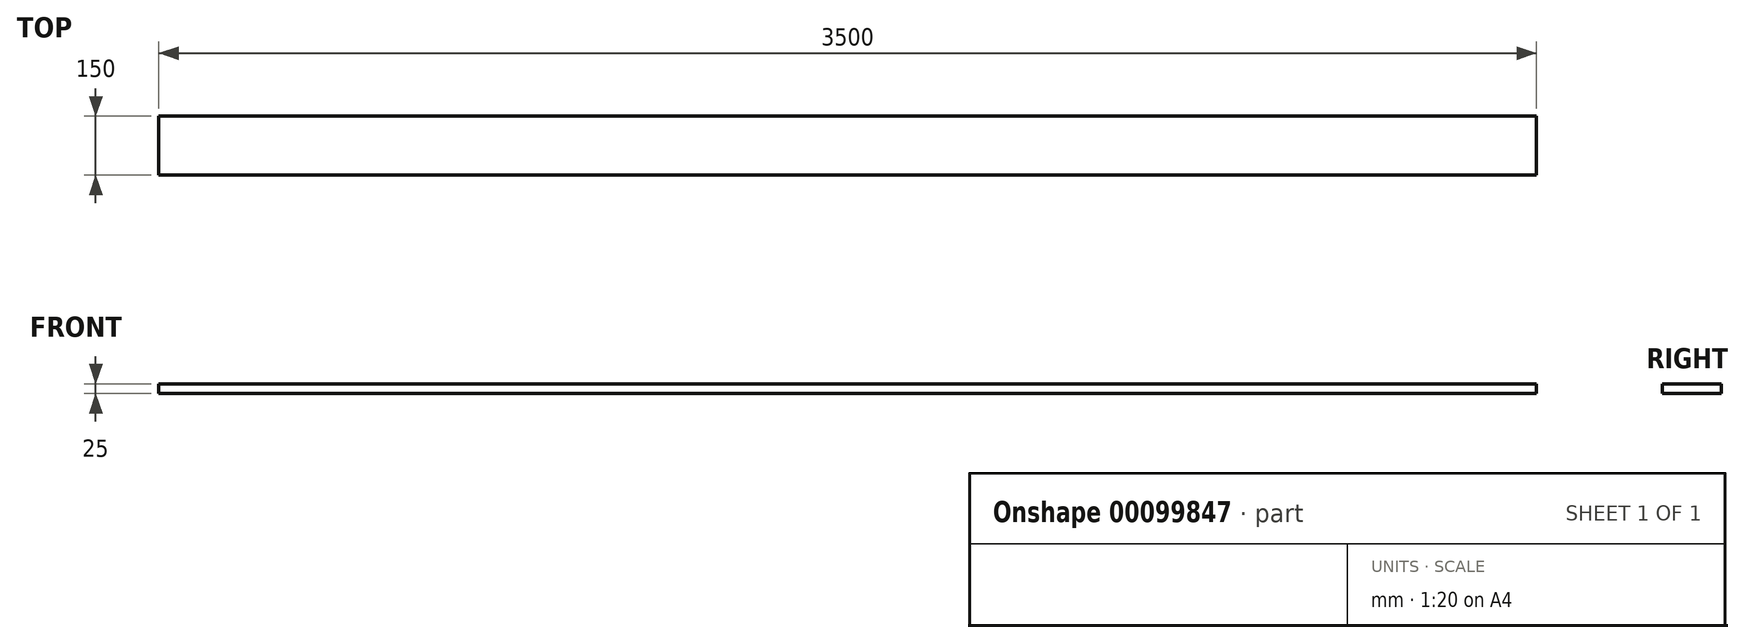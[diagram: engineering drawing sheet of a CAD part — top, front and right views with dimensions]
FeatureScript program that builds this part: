
annotation { "Feature Type Name" : "Feature", "Feature Type Description" : "" }
export const myFeature = defineFeature(function(context is Context, id is Id, definition is map)
    precondition{}
    {
        {
            var Q0;
            Q0=qCreatedBy(makeId("Top.planeOp"),FACE);
            var sketch = newSketch(context, id + "F0", { "sketchPlane" : qUnion([Q0])});
            skLineSegment(sketch, "E0.bottom", {"start": v(-1750, 0) * mm, "end": v(1750, 0) * mm});
            skLineSegment(sketch, "E0.top", {"start": v(-1750, -150) * mm, "end": v(1750, -150) * mm});
            skLineSegment(sketch, "E0.left", {"start": v(-1750, 0) * mm, "end": v(-1750, -150) * mm});
            skLineSegment(sketch, "E0.right", {"start": v(1750, 0) * mm, "end": v(1750, -150) * mm});
            skSolve(sketch);
        }
        {
            var Q0;
            Q0 = qSketchRegion(id + "F0", true);
            extrude(context, id + "F1", {"entities" : qUnion([Q0]), "depth" : 25 * mm});
        }
    });
